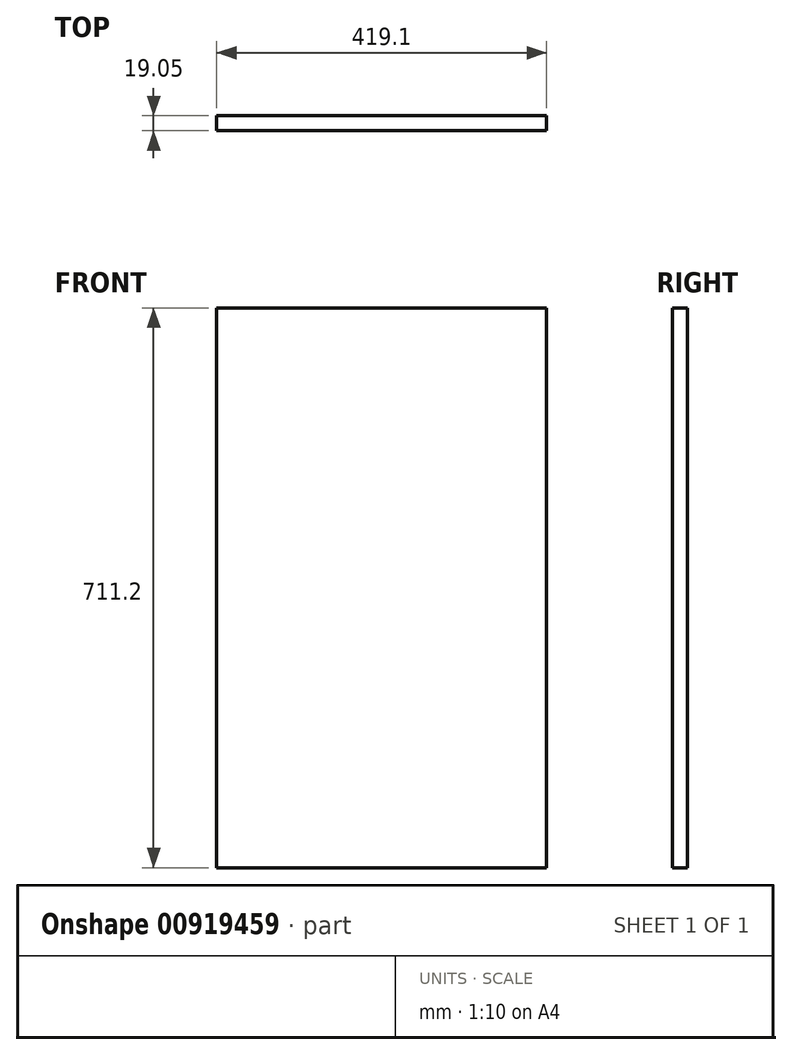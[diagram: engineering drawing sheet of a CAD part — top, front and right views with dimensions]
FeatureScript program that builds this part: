
annotation { "Feature Type Name" : "Feature", "Feature Type Description" : "" }
export const myFeature = defineFeature(function(context is Context, id is Id, definition is map)
    precondition{}
    {
        {
            var Q0;
            Q0=qCreatedBy(makeId("Front.planeOp"),FACE);
            var sketch = newSketch(context, id + "F0", { "sketchPlane" : qUnion([Q0])});
            skLineSegment(sketch, "E0.bottom", {"start": v(209.55, 355.6) * mm, "end": v(-209.55, 355.6) * mm});
            skLineSegment(sketch, "E0.top", {"start": v(209.55, -355.6) * mm, "end": v(-209.55, -355.6) * mm});
            skLineSegment(sketch, "E0.left", {"start": v(209.55, 355.6) * mm, "end": v(209.55, -355.6) * mm});
            skLineSegment(sketch, "E0.right", {"start": v(-209.55, 355.6) * mm, "end": v(-209.55, -355.6) * mm});
            skPoint(sketch, "E0.middle", {"position": v(0, 0) * mm});
            skSolve(sketch);
        }
        {
            var Q0;
            Q0=makeQuery(id+"F0.imprint","IMPRINT",FACE,{"disambiguationData":[TD([[makeQuery(id+"F0.imprint","IMPRINT",EDGE,{"derivedFrom":sQuery(id+"F0.wireOp",EDGE,"E0.bottom")}),1.0]])]});
            extrude(context, id + "F1", {"entities" : qUnion([Q0]), "depth" : 19.05 * mm, "offsetDistance" : 25.4 * mm});
        }
    });
